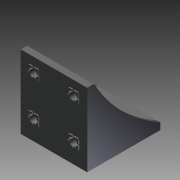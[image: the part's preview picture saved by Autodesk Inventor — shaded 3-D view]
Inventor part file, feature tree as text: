
AUTODESK INVENTOR PART (.ipt)
format: ipt  version: 2011 SP1 (Build 150282100, 282)  size: 300,032 bytes
history: native  units: mm
features: other x146, hole x42, extrude x13, sketch x7
ambient origin geometry x8: Origin, YZ Plane, XZ Plane, XY Plane, X Axis, Y Axis, Z Axis, Center Point
bodies: Solid1 (feature_tree)
feature tree (208):
  extrude  "Extrusion1"  Depth=45.0mm TaperAngle=0.0deg
  extrude  "Extrusion2"  Depth=5.0mm TaperAngle=0.0deg
  extrude  "Extrusion3"  Depth=5.0mm TaperAngle=0.0deg
  extrude  "Extrusion4"  Depth=5.0mm TaperAngle=0.0deg
  other  "Pattern_3_SKETCH_1"
  other  "Pattern_3_SKETCH_2"
  other  "Pattern_3_SKETCH_3"
  extrude  "Extrusion5"  Depth=5.0mm TaperAngle=0.0deg
  extrude  "Extrusion6"  Depth=0.8mm TaperAngle=0.0deg
  extrude  "Extrusion7"  [1 undecoded]
  extrude  "Extrusion8"  [1 undecoded]
  other  "Pattern_4_SKETCH_1"
  other  "Pattern_4_SKETCH_2"
  other  "Pattern_4_SKETCH_3"
  extrude  "Extrusion9"  [1 undecoded]
  extrude  "Extrusion10"  [1 undecoded]
  extrude  "Extrusion11"  [1 undecoded]
  extrude  "Extrusion12"  [1 undecoded]
  extrude  "Extrusion13"  [1 undecoded]
  other  "SD6_50_1_XY"
  other  "SD6_50_1_YZ"
  other  "SD6_50_1_ZX"
  other  "SD6_50_1_X"
  other  "SD6_50_1_Y"
  other  "SD6_50_1_Z"
  other  "SD6_50_1_Center"
  other  "SD6_50_2_XY"
  other  "SD6_50_2_YZ"
  other  "SD6_50_2_ZX"
  other  "SD6_50_2_X"
  other  "SD6_50_2_Y"
  other  "SD6_50_2_Z"
  other  "SD6_50_2_Center"
  other  "SD6_50_3_XY"
  other  "SD6_50_3_YZ"
  other  "SD6_50_3_ZX"
  other  "SD6_50_3_X"
  other  "SD6_50_3_Y"
  other  "SD6_50_3_Z"
  other  "SD6_50_3_Center"
  other  "SD6_50_4_XY"
  other  "SD6_50_4_YZ"
  other  "SD6_50_4_ZX"
  other  "SD6_50_4_X"
  other  "SD6_50_4_Y"
  other  "SD6_50_4_Z"
  other  "SD6_50_4_Center"
  other  "a10_to_bolt_XY"
  other  "a10_to_bolt_YZ"
  other  "a10_to_bolt_ZX"
  other  "a10_to_bolt_X"
  other  "a10_to_bolt_Y"
  other  "a10_to_bolt_Z"
  other  "a10_to_bolt_Center"
  other  "a11_to_bolt_XY"
  other  "a11_to_bolt_YZ"
  other  "a11_to_bolt_ZX"
  other  "a11_to_bolt_X"
  other  "a11_to_bolt_Y"
  other  "a11_to_bolt_Z"
  other  "a11_to_bolt_Center"
  other  "a12_to_bolt_XY"
  other  "a12_to_bolt_YZ"
  other  "a12_to_bolt_ZX"
  other  "a12_to_bolt_X"
  other  "a12_to_bolt_Y"
  other  "a12_to_bolt_Z"
  other  "a12_to_bolt_Center"
  other  "a13_to_bolt_XY"
  other  "a13_to_bolt_YZ"
  other  "a13_to_bolt_ZX"
  other  "a13_to_bolt_X"
  other  "a13_to_bolt_Y"
  other  "a13_to_bolt_Z"
  other  "a13_to_bolt_Center"
  other  "a14_to_bolt_XY"
  other  "a14_to_bolt_YZ"
  other  "a14_to_bolt_ZX"
  other  "a14_to_bolt_X"
  other  "a14_to_bolt_Y"
  other  "a14_to_bolt_Z"
  other  "a14_to_bolt_Center"
  other  "a1_to_bolt_XY"
  other  "a1_to_bolt_YZ"
  other  "a1_to_bolt_ZX"
  other  "a1_to_bolt_X"
  other  "a1_to_bolt_Y"
  other  "a1_to_bolt_Z"
  other  "a1_to_bolt_Center"
  other  "a2_to_bolt_XY"
  other  "a2_to_bolt_YZ"
  other  "a2_to_bolt_ZX"
  other  "a2_to_bolt_X"
  other  "a2_to_bolt_Y"
  other  "a2_to_bolt_Z"
  other  "a2_to_bolt_Center"
  other  "a3_to_bolt_XY"
  other  "a3_to_bolt_YZ"
  other  "a3_to_bolt_ZX"
  other  "a3_to_bolt_X"
  other  "a3_to_bolt_Y"
  other  "a3_to_bolt_Z"
  other  "a3_to_bolt_Center"
  other  "a4_to_bolt_XY"
  other  "a4_to_bolt_YZ"
  other  "a4_to_bolt_ZX"
  other  "a4_to_bolt_X"
  other  "a4_to_bolt_Y"
  other  "a4_to_bolt_Z"
  other  "a4_to_bolt_Center"
  other  "a55_to_bolt_XY"
  other  "a55_to_bolt_YZ"
  other  "a55_to_bolt_ZX"
  other  "a55_to_bolt_X"
  other  "a55_to_bolt_Y"
  other  "a55_to_bolt_Z"
  other  "a55_to_bolt_Center"
  other  "a5_to_bolt_XY"
  other  "a5_to_bolt_YZ"
  other  "a5_to_bolt_ZX"
  other  "a5_to_bolt_X"
  other  "a5_to_bolt_Y"
  other  "a5_to_bolt_Z"
  other  "a5_to_bolt_Center"
  other  "a6_to_bolt_XY"
  other  "a6_to_bolt_YZ"
  other  "a6_to_bolt_ZX"
  other  "a6_to_bolt_X"
  other  "a6_to_bolt_Y"
  other  "a6_to_bolt_Z"
  other  "a6_to_bolt_Center"
  other  "a7_to_bolt_XY"
  other  "a7_to_bolt_YZ"
  other  "a7_to_bolt_ZX"
  other  "a7_to_bolt_X"
  other  "a7_to_bolt_Y"
  other  "a7_to_bolt_Z"
  other  "a7_to_bolt_Center"
  other  "a8_to_bolt_XY"
  other  "a8_to_bolt_YZ"
  other  "a8_to_bolt_ZX"
  other  "a8_to_bolt_X"
  other  "a8_to_bolt_Y"
  other  "a8_to_bolt_Z"
  other  "a8_to_bolt_Center"
  other  "a9_to_bolt_XY"
  other  "a9_to_bolt_YZ"
  other  "a9_to_bolt_ZX"
  other  "a9_to_bolt_X"
  other  "a9_to_bolt_Y"
  other  "a9_to_bolt_Z"
  other  "a9_to_bolt_Center"
  other  "bracket_to_dummy_XY"
  other  "bracket_to_dummy_YZ"
  other  "bracket_to_dummy_ZX"
  other  "bracket_to_dummy_X"
  other  "bracket_to_dummy_Y"
  other  "bracket_to_dummy_Z"
  other  "bracket_to_dummy_Center"
  hole  "hole_x1_bolt_XY"  [1 undecoded]
  hole  "hole_x1_bolt_YZ"  [1 undecoded]
  hole  "hole_x1_bolt_ZX"  [1 undecoded]
  hole  "hole_x1_bolt_X"  [1 undecoded]
  hole  "hole_x1_bolt_Y"  [1 undecoded]
  hole  "hole_x1_bolt_Z"  [1 undecoded]
  hole  "hole_x1_bolt_Center"  [1 undecoded]
  hole  "holex2_to_bolt_XY"  [1 undecoded]
  hole  "holex2_to_bolt_YZ"  [1 undecoded]
  hole  "holex2_to_bolt_ZX"  [1 undecoded]
  hole  "holex2_to_bolt_X"  [1 undecoded]
  hole  "holex2_to_bolt_Y"  [1 undecoded]
  hole  "holex2_to_bolt_Z"  [1 undecoded]
  hole  "holex2_to_bolt_Center"  [1 undecoded]
  hole  "holex3_to_bolt_XY"  [1 undecoded]
  hole  "holex3_to_bolt_YZ"  [1 undecoded]
  hole  "holex3_to_bolt_ZX"  [1 undecoded]
  hole  "holex3_to_bolt_X"  [1 undecoded]
  hole  "holex3_to_bolt_Y"  [1 undecoded]
  hole  "holex3_to_bolt_Z"  [1 undecoded]
  hole  "holex3_to_bolt_Center"  [1 undecoded]
  hole  "holex4_to_bolt_XY"  [1 undecoded]
  hole  "holex4_to_bolt_YZ"  [1 undecoded]
  hole  "holex4_to_bolt_ZX"  [1 undecoded]
  hole  "holex4_to_bolt_X"  [1 undecoded]
  hole  "holex4_to_bolt_Y"  [1 undecoded]
  hole  "holex4_to_bolt_Z"  [1 undecoded]
  hole  "holex4_to_bolt_Center"  [1 undecoded]
  hole  "holex5_to_bolt_XY"  [1 undecoded]
  hole  "holex5_to_bolt_YZ"  [1 undecoded]
  hole  "holex5_to_bolt_ZX"  [1 undecoded]
  hole  "holex5_to_bolt_X"  [1 undecoded]
  hole  "holex5_to_bolt_Y"  [1 undecoded]
  hole  "holex5_to_bolt_Z"  [1 undecoded]
  hole  "holex5_to_bolt_Center"  [1 undecoded]
  hole  "holex6_to_bolt_XY"  [1 undecoded]
  hole  "holex6_to_bolt_YZ"  [1 undecoded]
  hole  "holex6_to_bolt_ZX"  [1 undecoded]
  hole  "holex6_to_bolt_X"  [1 undecoded]
  hole  "holex6_to_bolt_Y"  [1 undecoded]
  hole  "holex6_to_bolt_Z"  [1 undecoded]
  hole  "holex6_to_bolt_Center"  [1 undecoded]
  sketch  "Sketch_15"  dims[d16=5.0mm d17=0.0mm d18=5.0mm d19=0.0mm]
  sketch  "Sketch_16"  dims[d20=5.0mm d21=0.0mm d22=0.8mm d23=0.0mm]
  sketch  "Sketch_28"  dims[d24=0.8mm d25=0.0mm d26=0.0mm d27=0.0mm d28=0.0mm d29=0.0mm d30=0.0mm d31=0.0mm d32=0.0mm d33=0.0mm]
  sketch  "Sketch_22_ALT_Drilling_1"  dims[d0=50.0mm d1=0.0mm d2=45.0mm d3=0.0mm]
  sketch  "Sketch_24_ALT_Drilling_2"  dims[d8=5.0mm d9=0.0mm d10=5.0mm d11=0.0mm]
  sketch  "Sketch_1"  dims[d4=50.0mm d5=0.0mm d6=5.0mm d7=0.0mm]
  sketch  "Sketch_14"  dims[d12=5.0mm d13=0.0mm d14=5.0mm d15=0.0mm]
note: 49 required parameter values undecoded (feature->parameter linkage not recoverable at this tier; creation-order binding heuristic only, values carry confidence <= 0.55)
